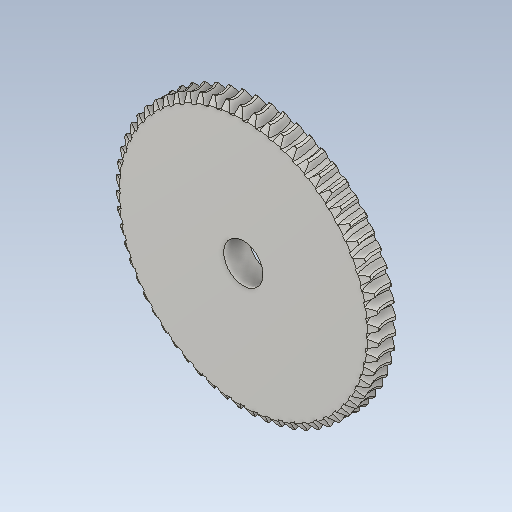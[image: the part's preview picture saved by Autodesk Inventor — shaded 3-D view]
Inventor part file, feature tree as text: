
AUTODESK INVENTOR PART (.ipt)
format: ipt  version: 2021 (Build 250183000, 183)  size: 1,150,464 bytes
history: native  units: mm (DEFAULTED — no unit token found)
features: other x8, plane x3, sketch x2, pattern_circular x1, extrude x1
ambient origin geometry x5: Origin, X Axis, Y Axis, Z Axis, Center Point
bodies: Solid1 (feature_tree)
feature tree (15):
  other  "Tooth Plane"
  other  "Base Body Sketch"
  other  "Base Body"
  other  "Base Body2"
  plane  "Work Plane13"
  other  "Tooth"
  pattern_circular  "Tooth Pattern"  [2 undecoded]
  plane  "Work Plane14"
  plane  "Work Plane15"
  extrude  "Extrusion1"  Depth=70.744372mm
  other  "Tooth Sketch"
  sketch  "Sketch8"  dims[d35=90.0deg]
  other  "Srf1"
  sketch  "Sketch9"  dims[d37=-0.996687mm d38=70.744372mm d39=3.490659mm d40=7.680818mm d41=10.106339mm d42=1.905mm d43=90.0deg d44=600.0mm d46=360.0deg d50=5.318254mm d68=70.744372mm d69=0.0mm d73=0.0mm d75=0.523599mm d77=121.276067mm d78=12.3mm d79=0.0mm d80=0.0mm d81=0.0mm d82=0.0mm d83=0.523599mm d84=0.0mm d85=180.0deg d86=70.744372mm d87=127.33987mm d89=16.170142mm d90=90.0deg d92=12.3mm d93=70.744372mm d94=19.05mm d95=0.0mm d96=0.0mm]
  other  "Pitch Diameter"
note: 2 required parameter values undecoded (feature->parameter linkage not recoverable at this tier; creation-order binding heuristic only, values carry confidence <= 0.55)
